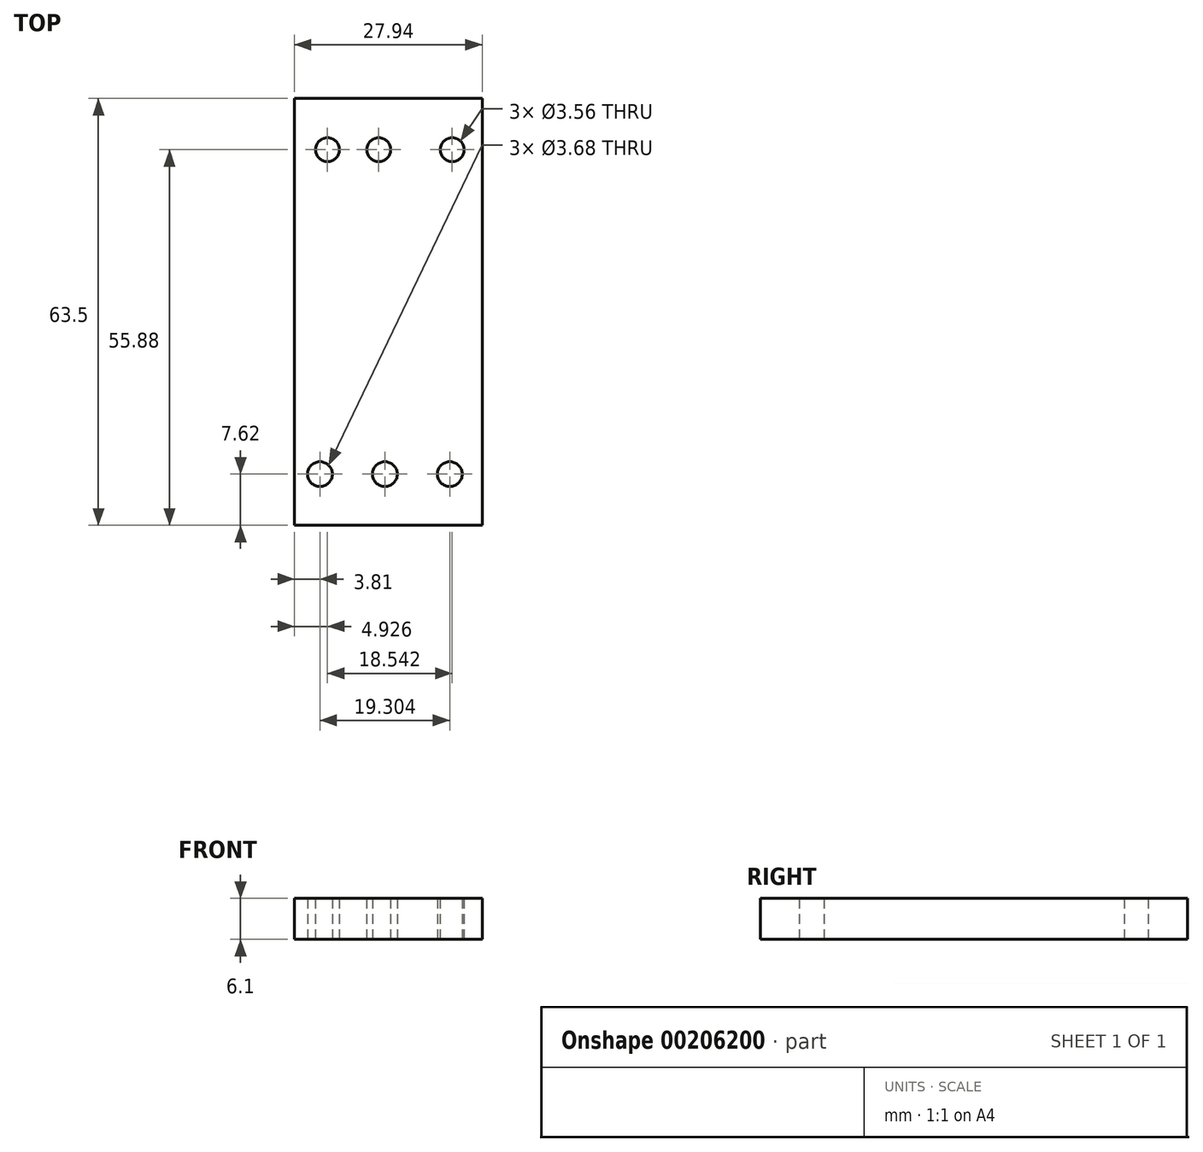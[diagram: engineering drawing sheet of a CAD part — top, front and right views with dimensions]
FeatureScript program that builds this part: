
annotation { "Feature Type Name" : "Feature", "Feature Type Description" : "" }
export const myFeature = defineFeature(function(context is Context, id is Id, definition is map)
    precondition{}
    {
        {
            var Q0;
            Q0=qCreatedBy(makeId("Top.planeOp"),FACE);
            var sketch = newSketch(context, id + "F0", { "sketchPlane" : qUnion([Q0])});
            skLineSegment(sketch, "E0.bottom", {"start": v(0, 0) * mm, "end": v(27.94, 0) * mm});
            skLineSegment(sketch, "E0.top", {"start": v(0, 63.5) * mm, "end": v(27.94, 63.5) * mm});
            skLineSegment(sketch, "E0.left", {"start": v(0, 0) * mm, "end": v(0, 63.5) * mm});
            skLineSegment(sketch, "E0.right", {"start": v(27.94, 0) * mm, "end": v(27.94, 63.5) * mm});
            skCircle(sketch, "E1", {"center": v(3.8, 7.62) * mm, "radius": 1.84 * mm});
            skCircle(sketch, "E2.1.0.0", {"center": v(13.46, 7.62) * mm, "radius": 1.84 * mm});
            skLineSegment(sketch, "E2.direction1", {"start": v(3.8, 7.62) * mm, "end": v(13.46, 7.62) * mm, "construction": true});
            skCircle(sketch, "E3.0.2.0", {"center": v(23.11, 7.62) * mm, "radius": 1.84 * mm});
            skCircle(sketch, "E4", {"center": v(4.93, 55.88) * mm, "radius": 1.78 * mm});
            skCircle(sketch, "E5.1.0.0", {"center": v(12.55, 55.88) * mm, "radius": 1.78 * mm});
            skLineSegment(sketch, "E5.direction1", {"start": v(4.93, 55.88) * mm, "end": v(12.55, 55.88) * mm, "construction": true});
            skCircle(sketch, "E6.1.0.0", {"center": v(23.47, 55.88) * mm, "radius": 1.78 * mm});
            skLineSegment(sketch, "E6.direction1", {"start": v(12.55, 55.88) * mm, "end": v(23.47, 55.88) * mm, "construction": true});
            skSolve(sketch);
        }
        {
            var Q0;
            Q0=qSketchRegion(id+"F0",true);
            extrude(context, id + "F1", {"entities" : qUnion([Q0]), "depth" : 6.1 * mm});
        }
    });
